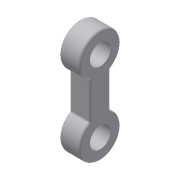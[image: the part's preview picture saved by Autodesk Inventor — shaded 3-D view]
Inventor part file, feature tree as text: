
AUTODESK INVENTOR PART (.ipt)
format: ipt  version: 2014 (Build 180170000, 170)  size: 168,960 bytes
history: native  units: mm
features: fillet x2, extrude x1, sketch x1
ambient origin geometry x8: Origin, YZ Plane, XZ Plane, XY Plane, X Axis, Y Axis, Z Axis, Center Point
bodies: Solid1 (feature_tree)
feature tree (4):
  extrude  "Extrusion1"  Depth=20.0mm
  fillet  "Fillet1"  Radius=40.0mm
  fillet  "Fillet2"  Radius=20.0mm
  sketch  "Sketch1"  dims[d0=70.0mm d1=20.0mm d2=40.0mm d3=20.0mm d4=20.0mm d5=0.0mm d6=2.0mm d7=2.0mm]
